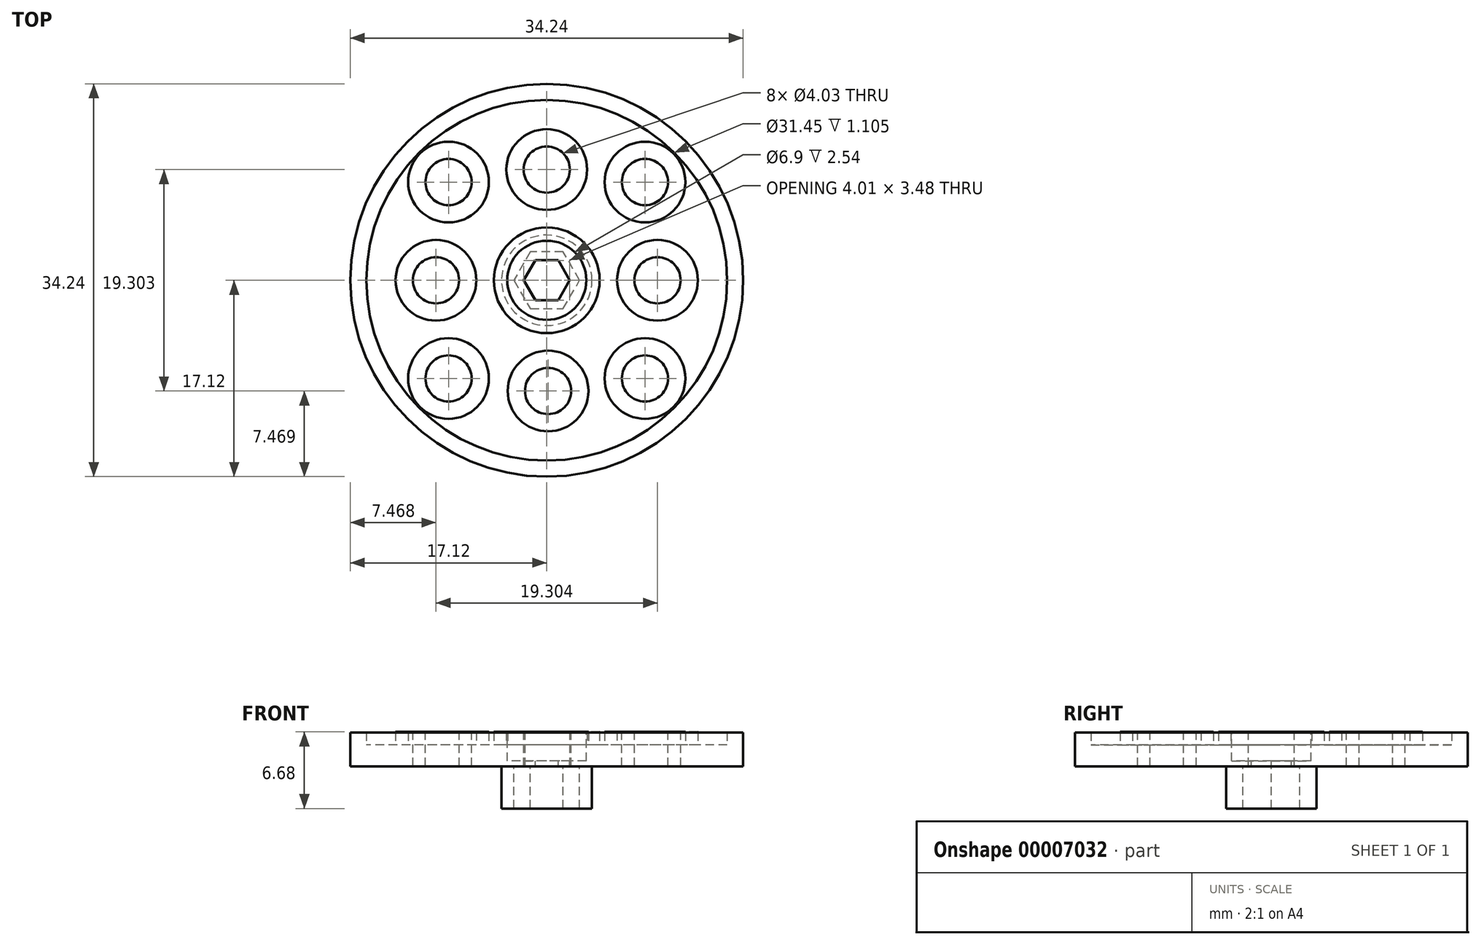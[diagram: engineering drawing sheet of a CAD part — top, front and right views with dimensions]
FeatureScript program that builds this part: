
annotation { "Feature Type Name" : "Feature", "Feature Type Description" : "" }
export const myFeature = defineFeature(function(context is Context, id is Id, definition is map)
    precondition{}
    {
        {
            var Q0;
            Q0=qCreatedBy(makeId("Top.planeOp"),FACE);
            var sketch = newSketch(context, id + "F0", { "sketchPlane" : qUnion([Q0])});
            skCircle(sketch, "E0", {"center": v(0, 0) * mm, "radius": 17.12 * mm});
            skCircle(sketch, "E1", {"center": v(0, 0) * mm, "radius": 15.72 * mm});
            skSolve(sketch);
        }
        {
            var Q0;
            Q0=makeQuery(id+"F0.imprint","IMPRINT",FACE,{"disambiguationData":[TD([[makeQuery(id+"F0.imprint","IMPRINT",EDGE,{"derivedFrom":sQuery(id+"F0.wireOp",EDGE,"E1")}),1.0]])]});
            var Q1;
            Q1=makeQuery(id+"F0.imprint","IMPRINT",FACE,{"disambiguationData":[TD([[makeQuery(id+"F0.imprint","IMPRINT",EDGE,{"derivedFrom":sQuery(id+"F0.wireOp",EDGE,"E0")}),1.0]])]});
            extrude(context, id + "F1", {"entities" : qUnion([Q0, Q1]), "depth" : 1.85 * mm});
        }
        {
            var Q0;
            Q0 = qSketchRegion(id + "F0", true);
            extrude(context, id + "F2", {"entities" : qUnion([Q0]), "operationType" : NewBodyOperationType.ADD, "depth" : 2.96 * mm});
        }
        {
            var Q0;
            Q0=makeQuery(id+"F1.opExtrude","CAP_FACE",FACE,{"disambiguationData":[OSD([sQuery(id+"F0.wireOp",EDGE,"E0")])],"isStart":false});
            var sketch = newSketch(context, id + "F3", { "sketchPlane" : qUnion([Q0])});
            skCircle(sketch, "E2", {"center": v(-8.56, 8.56) * mm, "radius": 3.52 * mm});
            skCircle(sketch, "E3", {"center": v(0, 9.65) * mm, "radius": 3.52 * mm});
            skCircle(sketch, "E4", {"center": v(8.56, 8.56) * mm, "radius": 3.52 * mm});
            skCircle(sketch, "E5", {"center": v(8.56, -8.56) * mm, "radius": 3.52 * mm});
            skCircle(sketch, "E6", {"center": v(-8.56, -8.56) * mm, "radius": 3.52 * mm});
            skCircle(sketch, "E7", {"center": v(-9.65, 0) * mm, "radius": 3.52 * mm});
            skCircle(sketch, "E8", {"center": v(0.12, -9.65) * mm, "radius": 3.52 * mm});
            skCircle(sketch, "E9", {"center": v(0, 0) * mm, "radius": 4.61 * mm});
            skCircle(sketch, "E10", {"center": v(9.65, 0) * mm, "radius": 3.52 * mm});
            skLineSegment(sketch, "E11", {"start": v(0, 0) * mm, "end": v(0, -17.12) * mm, "construction": true});
            skLineSegment(sketch, "E12", {"start": v(0, 0) * mm, "end": v(0, 17.12) * mm, "construction": true});
            skLineSegment(sketch, "E13", {"start": v(0, 0) * mm, "end": v(17.12, 0) * mm, "construction": true});
            skLineSegment(sketch, "E14", {"start": v(0, 0) * mm, "end": v(-17.12, 0) * mm, "construction": true});
            skLineSegment(sketch, "E15", {"start": v(0, 17.12) * mm, "end": v(17.12, 0) * mm, "construction": true});
            skLineSegment(sketch, "E16", {"start": v(0, -17.12) * mm, "end": v(17.12, 0) * mm, "construction": true});
            skLineSegment(sketch, "E17", {"start": v(0, -17.12) * mm, "end": v(-17.12, 0) * mm, "construction": true});
            skLineSegment(sketch, "E18", {"start": v(0, 17.12) * mm, "end": v(-17.12, 0) * mm, "construction": true});
            skLineSegment(sketch, "E19", {"start": v(8.56, -8.56) * mm, "end": v(8.56, 8.56) * mm});
            skLineSegment(sketch, "E20", {"start": v(-8.56, 8.56) * mm, "end": v(8.56, 8.56) * mm});
            skLineSegment(sketch, "E21", {"start": v(-8.56, -8.56) * mm, "end": v(8.56, -8.56) * mm});
            skLineSegment(sketch, "E22", {"start": v(-8.56, -8.56) * mm, "end": v(-8.56, 8.56) * mm});
            skSolve(sketch);
        }
        {
            var Q0;
            {var subQ1=sQuery(id+"F3.wireOp",EDGE,"E2");var subQ3=sQuery(id+"F3.wireOp",EDGE,"E20");var subQ5=makeQuery(id+"F3.imprint","INTERSECT",VERTEX,{"derivedFrom":[subQ1,subQ3]});Q0=makeQuery(id+"F3.imprint","IMPRINT",FACE,{"disambiguationData":[TD([[makeQuery(id+"F3.imprint","IMPRINT",EDGE,{"disambiguationData":[TD([[subQ5,-1.0]])],"derivedFrom":subQ1}),1.0]])]});}
            var Q1;
            {var subQ0=sQuery(id+"F3.wireOp",EDGE,"E20");var subQ1=sQuery(id+"F3.wireOp",EDGE,"E2");var subQ2=makeQuery(id+"F3.imprint","INTERSECT",VERTEX,{"derivedFrom":[subQ1,subQ0]});Q1=makeQuery(id+"F3.imprint","IMPRINT",FACE,{"disambiguationData":[TD([[makeQuery(id+"F3.imprint","IMPRINT",EDGE,{"disambiguationData":[TD([[subQ2,1.0]])],"derivedFrom":subQ1}),1.0]])]});}
            var Q2;
            {var subQ0=sQuery(id+"F3.wireOp",EDGE,"E20");var subQ1=sQuery(id+"F3.wireOp",EDGE,"E3");var subQ3=makeQuery(id+"F3.imprint","INTERSECT",VERTEX,{"disambiguationData":[OD(0.0)],"derivedFrom":[subQ1,subQ0]});Q2=makeQuery(id+"F3.imprint","IMPRINT",FACE,{"disambiguationData":[TD([[makeQuery(id+"F3.imprint","IMPRINT",EDGE,{"disambiguationData":[TD([[subQ3,1.0]])],"derivedFrom":subQ1}),1.0]])]});}
            var Q3;
            {var subQ1=sQuery(id+"F3.wireOp",EDGE,"E4");var subQ3=sQuery(id+"F3.wireOp",EDGE,"E19");var subQ5=makeQuery(id+"F3.imprint","INTERSECT",VERTEX,{"derivedFrom":[subQ1,subQ3]});Q3=makeQuery(id+"F3.imprint","IMPRINT",FACE,{"disambiguationData":[TD([[makeQuery(id+"F3.imprint","IMPRINT",EDGE,{"disambiguationData":[TD([[subQ5,1.0]])],"derivedFrom":subQ1}),1.0]])]});}
            var Q4;
            {var subQ1=sQuery(id+"F3.wireOp",EDGE,"E4");var subQ3=sQuery(id+"F3.wireOp",EDGE,"E19");var subQ5=makeQuery(id+"F3.imprint","INTERSECT",VERTEX,{"derivedFrom":[subQ1,subQ3]});Q4=makeQuery(id+"F3.imprint","IMPRINT",FACE,{"disambiguationData":[TD([[makeQuery(id+"F3.imprint","IMPRINT",EDGE,{"disambiguationData":[TD([[subQ5,-1.0]])],"derivedFrom":subQ1}),1.0]])]});}
            var Q5;
            {var subQ1=sQuery(id+"F3.wireOp",EDGE,"E5");var subQ3=sQuery(id+"F3.wireOp",EDGE,"E19");var subQ5=makeQuery(id+"F3.imprint","INTERSECT",VERTEX,{"derivedFrom":[subQ1,subQ3]});Q5=makeQuery(id+"F3.imprint","IMPRINT",FACE,{"disambiguationData":[TD([[makeQuery(id+"F3.imprint","IMPRINT",EDGE,{"disambiguationData":[TD([[subQ5,1.0]])],"derivedFrom":subQ1}),1.0]])]});}
            var Q6;
            {var subQ1=sQuery(id+"F3.wireOp",EDGE,"E6");var subQ3=sQuery(id+"F3.wireOp",EDGE,"E21");var subQ5=makeQuery(id+"F3.imprint","INTERSECT",VERTEX,{"derivedFrom":[subQ1,subQ3]});Q6=makeQuery(id+"F3.imprint","IMPRINT",FACE,{"disambiguationData":[TD([[makeQuery(id+"F3.imprint","IMPRINT",EDGE,{"disambiguationData":[TD([[subQ5,1.0]])],"derivedFrom":subQ1}),1.0]])]});}
            var Q7;
            {var subQ0=sQuery(id+"F3.wireOp",EDGE,"E22");var subQ1=sQuery(id+"F3.wireOp",EDGE,"E7");var subQ3=makeQuery(id+"F3.imprint","INTERSECT",VERTEX,{"disambiguationData":[OD(0.0)],"derivedFrom":[subQ1,subQ0]});Q7=makeQuery(id+"F3.imprint","IMPRINT",FACE,{"disambiguationData":[TD([[makeQuery(id+"F3.imprint","IMPRINT",EDGE,{"disambiguationData":[TD([[subQ3,1.0]])],"derivedFrom":subQ1}),1.0]])]});}
            var Q8;
            {var subQ0=sQuery(id+"F3.wireOp",EDGE,"E21");var subQ1=sQuery(id+"F3.wireOp",EDGE,"E8");var subQ3=makeQuery(id+"F3.imprint","INTERSECT",VERTEX,{"disambiguationData":[OD(0.0)],"derivedFrom":[subQ1,subQ0]});Q8=makeQuery(id+"F3.imprint","IMPRINT",FACE,{"disambiguationData":[TD([[makeQuery(id+"F3.imprint","IMPRINT",EDGE,{"disambiguationData":[TD([[subQ3,1.0]])],"derivedFrom":subQ1}),1.0]])]});}
            var Q9;
            {var subQ0=sQuery(id+"F3.wireOp",EDGE,"E21");var subQ1=sQuery(id+"F3.wireOp",EDGE,"E8");var subQ3=makeQuery(id+"F3.imprint","INTERSECT",VERTEX,{"disambiguationData":[OD(0.0)],"derivedFrom":[subQ1,subQ0]});Q9=makeQuery(id+"F3.imprint","IMPRINT",FACE,{"disambiguationData":[TD([[makeQuery(id+"F3.imprint","IMPRINT",EDGE,{"disambiguationData":[TD([[subQ3,-1.0]])],"derivedFrom":subQ1}),1.0]])]});}
            var Q10;
            {var subQ0=sQuery(id+"F3.wireOp",EDGE,"E19");var subQ1=sQuery(id+"F3.wireOp",EDGE,"E10");var subQ3=makeQuery(id+"F3.imprint","INTERSECT",VERTEX,{"disambiguationData":[OD(0.0)],"derivedFrom":[subQ1,subQ0]});Q10=makeQuery(id+"F3.imprint","IMPRINT",FACE,{"disambiguationData":[TD([[makeQuery(id+"F3.imprint","IMPRINT",EDGE,{"disambiguationData":[TD([[subQ3,-1.0]])],"derivedFrom":subQ1}),1.0]])]});}
            var Q11;
            Q11=makeQuery(id+"F3.imprint","IMPRINT",FACE,{"disambiguationData":[TD([[makeQuery(id+"F3.imprint","IMPRINT",EDGE,{"derivedFrom":sQuery(id+"F3.wireOp",EDGE,"E9")}),1.0]])]});
            var Q12;
            {var subQ0=sQuery(id+"F3.wireOp",EDGE,"E22");var subQ1=sQuery(id+"F3.wireOp",EDGE,"E7");var subQ3=makeQuery(id+"F3.imprint","INTERSECT",VERTEX,{"disambiguationData":[OD(0.0)],"derivedFrom":[subQ1,subQ0]});Q12=makeQuery(id+"F3.imprint","IMPRINT",FACE,{"disambiguationData":[TD([[makeQuery(id+"F3.imprint","IMPRINT",EDGE,{"disambiguationData":[TD([[subQ3,-1.0]])],"derivedFrom":subQ1}),1.0]])]});}
            var Q13;
            {var subQ0=sQuery(id+"F3.wireOp",EDGE,"E20");var subQ1=sQuery(id+"F3.wireOp",EDGE,"E3");var subQ3=makeQuery(id+"F3.imprint","INTERSECT",VERTEX,{"disambiguationData":[OD(0.0)],"derivedFrom":[subQ1,subQ0]});Q13=makeQuery(id+"F3.imprint","IMPRINT",FACE,{"disambiguationData":[TD([[makeQuery(id+"F3.imprint","IMPRINT",EDGE,{"disambiguationData":[TD([[subQ3,-1.0]])],"derivedFrom":subQ1}),1.0]])]});}
            var Q14;
            {var subQ1=sQuery(id+"F3.wireOp",EDGE,"E6");var subQ3=sQuery(id+"F3.wireOp",EDGE,"E21");var subQ5=makeQuery(id+"F3.imprint","INTERSECT",VERTEX,{"derivedFrom":[subQ1,subQ3]});Q14=makeQuery(id+"F3.imprint","IMPRINT",FACE,{"disambiguationData":[TD([[makeQuery(id+"F3.imprint","IMPRINT",EDGE,{"disambiguationData":[TD([[subQ5,-1.0]])],"derivedFrom":subQ1}),1.0]])]});}
            var Q15;
            {var subQ0=sQuery(id+"F3.wireOp",EDGE,"E19");var subQ1=sQuery(id+"F3.wireOp",EDGE,"E10");var subQ3=makeQuery(id+"F3.imprint","INTERSECT",VERTEX,{"disambiguationData":[OD(0.0)],"derivedFrom":[subQ1,subQ0]});Q15=makeQuery(id+"F3.imprint","IMPRINT",FACE,{"disambiguationData":[TD([[makeQuery(id+"F3.imprint","IMPRINT",EDGE,{"disambiguationData":[TD([[subQ3,1.0]])],"derivedFrom":subQ1}),1.0]])]});}
            var Q16;
            {var subQ1=sQuery(id+"F3.wireOp",EDGE,"E5");var subQ3=sQuery(id+"F3.wireOp",EDGE,"E19");var subQ5=makeQuery(id+"F3.imprint","INTERSECT",VERTEX,{"derivedFrom":[subQ1,subQ3]});Q16=makeQuery(id+"F3.imprint","IMPRINT",FACE,{"disambiguationData":[TD([[makeQuery(id+"F3.imprint","IMPRINT",EDGE,{"disambiguationData":[TD([[subQ5,-1.0]])],"derivedFrom":subQ1}),1.0]])]});}
            extrude(context, id + "F4", {"entities" : qUnion([Q0, Q1, Q2, Q3, Q4, Q5, Q6, Q7, Q8, Q9, Q10, Q11, Q12, Q13, Q14, Q15, Q16]), "operationType" : NewBodyOperationType.ADD, "depth" : 1.14 * mm});
        }
        {
            var Q0;
            Q0=makeQuery(id+"F4.opExtrude","CAP_FACE",FACE,{"disambiguationData":[OSD([sQuery(id+"F3.wireOp",EDGE,"E9")])],"isStart":false});
            var sketch = newSketch(context, id + "F5", { "sketchPlane" : qUnion([Q0])});
            skCircle(sketch, "E23", {"center": v(8.56, 8.56) * mm, "radius": 2.01 * mm});
            skCircle(sketch, "E24", {"center": v(0, 9.65) * mm, "radius": 2.01 * mm});
            skCircle(sketch, "E25", {"center": v(-8.56, 8.56) * mm, "radius": 2.01 * mm});
            skCircle(sketch, "E26", {"center": v(-9.65, 0) * mm, "radius": 2.01 * mm});
            skCircle(sketch, "E27", {"center": v(-8.56, -8.56) * mm, "radius": 2.01 * mm});
            skCircle(sketch, "E28", {"center": v(0.12, -9.65) * mm, "radius": 2.01 * mm});
            skCircle(sketch, "E29", {"center": v(8.56, -8.56) * mm, "radius": 2.01 * mm});
            skCircle(sketch, "E30", {"center": v(9.65, 0) * mm, "radius": 2.01 * mm});
            skCircle(sketch, "E31", {"center": v(0, 0) * mm, "radius": 3.4 * mm});
            skSolve(sketch);
        }
        {
            var Q0;
            Q0=makeQuery(id+"F5.imprint","IMPRINT",FACE,{"disambiguationData":[TD([[makeQuery(id+"F5.imprint","IMPRINT",EDGE,{"derivedFrom":sQuery(id+"F5.wireOp",EDGE,"E23")}),1.0]])]});
            var Q1;
            Q1=makeQuery(id+"F5.imprint","IMPRINT",FACE,{"disambiguationData":[TD([[makeQuery(id+"F5.imprint","IMPRINT",EDGE,{"derivedFrom":sQuery(id+"F5.wireOp",EDGE,"E24")}),1.0]])]});
            var Q2;
            Q2=makeQuery(id+"F5.imprint","IMPRINT",FACE,{"disambiguationData":[TD([[makeQuery(id+"F5.imprint","IMPRINT",EDGE,{"derivedFrom":sQuery(id+"F5.wireOp",EDGE,"E25")}),1.0]])]});
            var Q3;
            Q3=makeQuery(id+"F5.imprint","IMPRINT",FACE,{"disambiguationData":[TD([[makeQuery(id+"F5.imprint","IMPRINT",EDGE,{"derivedFrom":sQuery(id+"F5.wireOp",EDGE,"E26")}),1.0]])]});
            var Q4;
            Q4=makeQuery(id+"F5.imprint","IMPRINT",FACE,{"disambiguationData":[TD([[makeQuery(id+"F5.imprint","IMPRINT",EDGE,{"derivedFrom":sQuery(id+"F5.wireOp",EDGE,"E27")}),1.0]])]});
            var Q5;
            Q5=makeQuery(id+"F5.imprint","IMPRINT",FACE,{"disambiguationData":[TD([[makeQuery(id+"F5.imprint","IMPRINT",EDGE,{"derivedFrom":sQuery(id+"F5.wireOp",EDGE,"E28")}),1.0]])]});
            var Q6;
            Q6=makeQuery(id+"F5.imprint","IMPRINT",FACE,{"disambiguationData":[TD([[makeQuery(id+"F5.imprint","IMPRINT",EDGE,{"derivedFrom":sQuery(id+"F5.wireOp",EDGE,"E29")}),1.0]])]});
            var Q7;
            Q7=makeQuery(id+"F5.imprint","IMPRINT",FACE,{"disambiguationData":[TD([[makeQuery(id+"F5.imprint","IMPRINT",EDGE,{"derivedFrom":sQuery(id+"F5.wireOp",EDGE,"E30")}),1.0]])]});
            extrude(context, id + "F6", {"entities" : qUnion([Q0, Q1, Q2, Q3, Q4, Q5, Q6, Q7]), "operationType" : NewBodyOperationType.REMOVE, "oppositeDirection" : true, "depth" : 3.05 * mm});
        }
        {
            var Q0;
            Q0=makeQuery(id+"F4.opExtrude","CAP_FACE",FACE,{"disambiguationData":[OSD([sQuery(id+"F3.wireOp",EDGE,"E9")])],"isStart":false});
            var sketch = newSketch(context, id + "F7", { "sketchPlane" : qUnion([Q0])});
            skCircle(sketch, "E32", {"center": v(0, 0) * mm, "radius": 3.45 * mm});
            skCircle(sketch, "E33.cCircle", {"center": v(0, 0) * mm, "radius": 1.74 * mm, "construction": true});
            skLineSegment(sketch, "E33.0", {"start": v(1, -1.74) * mm, "end": v(-1, -1.74) * mm});
            skLineSegment(sketch, "E33.1", {"start": v(-1, -1.74) * mm, "end": v(-2, 0) * mm});
            skLineSegment(sketch, "E33.2", {"start": v(-2, 0) * mm, "end": v(-1, 1.74) * mm});
            skLineSegment(sketch, "E33.3", {"start": v(-1, 1.74) * mm, "end": v(1, 1.74) * mm});
            skLineSegment(sketch, "E33.4", {"start": v(1, 1.74) * mm, "end": v(2, 0) * mm});
            skLineSegment(sketch, "E33.5", {"start": v(2, 0) * mm, "end": v(1, -1.74) * mm});
            skPoint(sketch, "E33.0.midPoint", {"position": v(0, -1.74) * mm});
            skSolve(sketch);
        }
        {
            var Q0;
            Q0=makeQuery(id+"F7.imprint","IMPRINT",FACE,{"disambiguationData":[TD([[makeQuery(id+"F7.imprint","IMPRINT",EDGE,{"derivedFrom":sQuery(id+"F7.wireOp",EDGE,"E33.0")}),-1.0]])]});
            extrude(context, id + "F8", {"entities" : qUnion([Q0]), "operationType" : NewBodyOperationType.REMOVE, "oppositeDirection" : true, "depth" : 6.86 * mm});
        }
        {
            var Q0;
            Q0 = qSketchRegion(id + "F7", true);
            extrude(context, id + "F9", {"entities" : qUnion([Q0]), "operationType" : NewBodyOperationType.REMOVE, "oppositeDirection" : true, "depth" : 2.54 * mm});
        }
        {
            var Q0;
            Q0=makeQuery(id+"F1.opExtrude","CAP_FACE",FACE,{"disambiguationData":[OSD([sQuery(id+"F0.wireOp",EDGE,"E0")])],"isStart":true});
            var sketch = newSketch(context, id + "F10", { "sketchPlane" : qUnion([Q0])});
            skCircle(sketch, "E34", {"center": v(0, 0) * mm, "radius": 3.94 * mm});
            skCircle(sketch, "E35.cCircle", {"center": v(0, 0) * mm, "radius": 2.48 * mm, "construction": true});
            skLineSegment(sketch, "E35.0", {"start": v(-1.43, -2.48) * mm, "end": v(-2.86, 0) * mm});
            skLineSegment(sketch, "E35.1", {"start": v(-2.86, 0) * mm, "end": v(-1.43, 2.48) * mm});
            skLineSegment(sketch, "E35.2", {"start": v(-1.43, 2.48) * mm, "end": v(1.43, 2.48) * mm});
            skLineSegment(sketch, "E35.3", {"start": v(1.43, 2.48) * mm, "end": v(2.86, 0) * mm});
            skLineSegment(sketch, "E35.4", {"start": v(2.86, 0) * mm, "end": v(1.43, -2.48) * mm});
            skLineSegment(sketch, "E35.5", {"start": v(1.43, -2.48) * mm, "end": v(-1.43, -2.48) * mm});
            skLineSegment(sketch, "E36", {"start": v(0, 0) * mm, "end": v(0, -2.48) * mm, "construction": true});
            skSolve(sketch);
        }
        {
            var Q0;
            Q0 = qSketchRegion(id + "F10", true);
            extrude(context, id + "F11", {"entities" : qUnion([Q0]), "operationType" : NewBodyOperationType.ADD, "depth" : 3.68 * mm});
        }
    });
